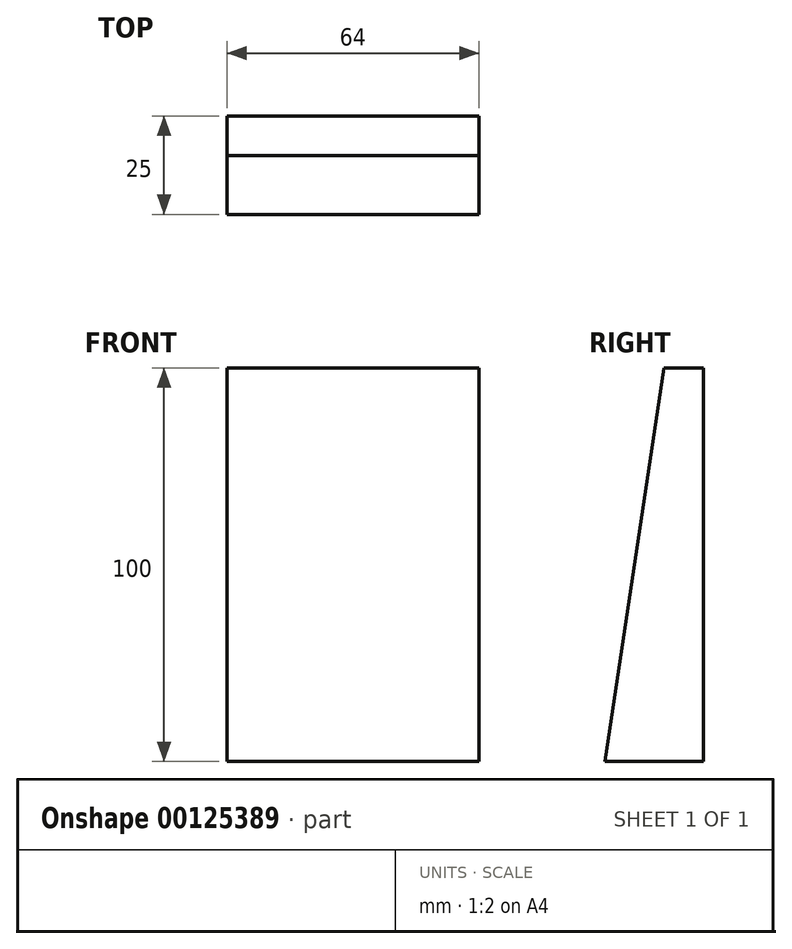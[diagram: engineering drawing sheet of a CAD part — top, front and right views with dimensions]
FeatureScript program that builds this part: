
annotation { "Feature Type Name" : "Feature", "Feature Type Description" : "" }
export const myFeature = defineFeature(function(context is Context, id is Id, definition is map)
    precondition{}
    {
        {
            var Q0;
            Q0=qCreatedBy(makeId("Right.planeOp"),FACE);
            var sketch = newSketch(context, id + "F0", { "sketchPlane" : qUnion([Q0])});
            skLineSegment(sketch, "E0", {"start": v(0, 54.82) * mm, "end": v(0, -45.18) * mm});
            skLineSegment(sketch, "E1", {"start": v(0, -45.18) * mm, "end": v(-25, -45.18) * mm});
            skLineSegment(sketch, "E2", {"start": v(-25, -45.18) * mm, "end": v(-10, 54.82) * mm});
            skLineSegment(sketch, "E3", {"start": v(-10, 54.82) * mm, "end": v(0, 54.82) * mm});
            skSolve(sketch);
        }
        {
            var Q0;
            Q0 = qSketchRegion(id + "F0", true);
            extrude(context, id + "F1", {"entities" : qUnion([Q0]), "endBound" : BoundingType.SYMMETRIC, "depth" : 64 * mm});
        }
    });
